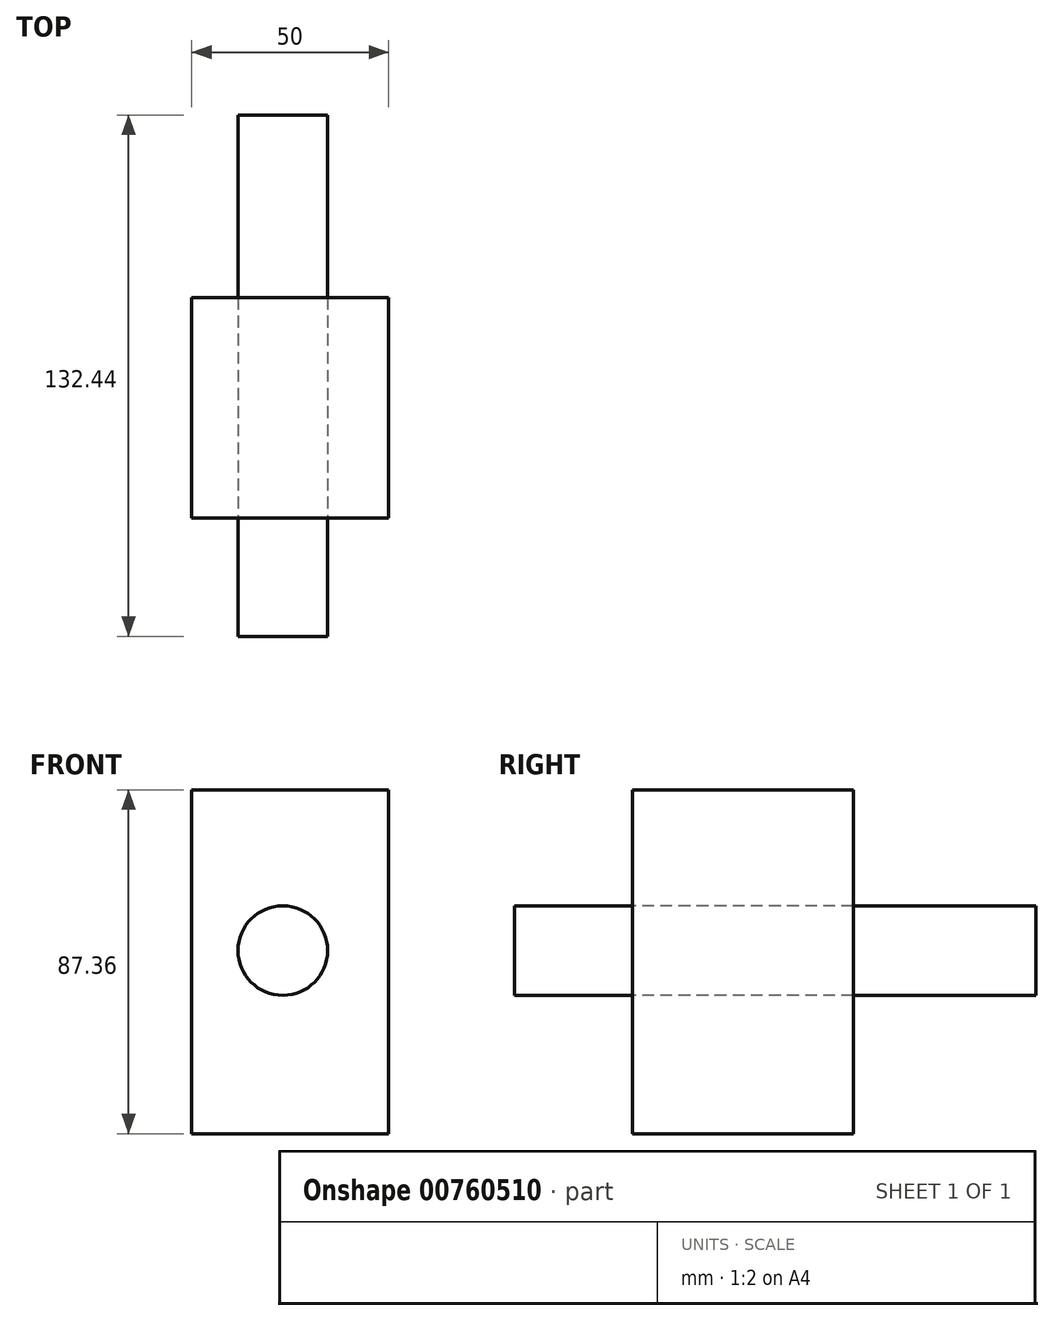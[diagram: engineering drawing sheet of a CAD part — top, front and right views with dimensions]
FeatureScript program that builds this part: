
annotation { "Feature Type Name" : "Feature", "Feature Type Description" : "" }
export const myFeature = defineFeature(function(context is Context, id is Id, definition is map)
    precondition{}
    {
        {
            var Q0;
            Q0=qCreatedBy(makeId("Right.planeOp"),FACE);
            var sketch = newSketch(context, id + "F0", { "sketchPlane" : qUnion([Q0])});
            skLineSegment(sketch, "E0.bottom", {"start": v(-25.06, 35.46) * mm, "end": v(31, 35.46) * mm});
            skLineSegment(sketch, "E0.top", {"start": v(-25.06, -31.9) * mm, "end": v(31, -31.9) * mm});
            skLineSegment(sketch, "E0.left", {"start": v(-25.06, 35.46) * mm, "end": v(-25.06, -31.9) * mm});
            skLineSegment(sketch, "E0.right", {"start": v(31, 35.46) * mm, "end": v(31, -31.9) * mm});
            skSolve(sketch);
        }
        {
            var Q0;
            Q0=makeQuery(id+"F0.imprint","IMPRINT",FACE,{"disambiguationData":[TD([[makeQuery(id+"F0.imprint","IMPRINT",EDGE,{"derivedFrom":sQuery(id+"F0.wireOp",EDGE,"E0.bottom")}),-1.0]])]});
            extrude(context, id + "F1", {"entities" : qUnion([Q0]), "depth" : 50 * mm, "offsetDistance" : 25 * mm});
        }
        {
            var Q0;
            Q0=makeQuery(id+"F1.opExtrude","SWEPT_FACE",FACE,{"disambiguationData":[OSD([sQuery(id+"F0.wireOp",EDGE,"E0.bottom")])]});
            extrude(context, id + "F2", {"entities" : qUnion([Q0]), "operationType" : NewBodyOperationType.ADD, "depth" : 20 * mm, "offsetDistance" : 25 * mm});
        }
        {
            var Q0;
            {var subQ0=sQuery(id+"F0.wireOp",EDGE,"E0.left");Q0=makeQuery(id+"F2.boolean.opBoolean","MERGE",FACE,{"derivedFrom":[makeQuery(id+"F1.opExtrude","SWEPT_FACE",FACE,{"disambiguationData":[OSD([subQ0])]}),makeQuery(id+"F2.opExtrude","SWEPT_FACE",FACE,{"disambiguationData":[OSD([sQuery(id+"F0.wireOp",EDGE,"E0.bottom"),subQ0])]})]});}
            var sketch = newSketch(context, id + "F3", { "sketchPlane" : qUnion([Q0])});
            skCircle(sketch, "E1", {"center": v(23.15, 14.6) * mm, "radius": 11.36 * mm});
            skSolve(sketch);
        }
        {
            var Q0;
            Q0 = qSketchRegion(id + "F3", true);
            extrude(context, id + "F4", {"entities" : qUnion([Q0]), "operationType" : NewBodyOperationType.ADD, "depth" : 30 * mm, "offsetDistance" : 25 * mm});
        }
        {
            var Q0;
            {var subQ0=sQuery(id+"F0.wireOp",EDGE,"E0.left");Q0=makeQuery(id+"F2.boolean.opBoolean","MERGE",FACE,{"derivedFrom":[makeQuery(id+"F1.opExtrude","SWEPT_FACE",FACE,{"disambiguationData":[OSD([subQ0])]}),makeQuery(id+"F2.opExtrude","SWEPT_FACE",FACE,{"disambiguationData":[OSD([sQuery(id+"F0.wireOp",EDGE,"E0.bottom"),subQ0])]})]});}
            var Q1;
            Q1=qCreatedBy(makeId("Front.planeOp"),FACE);
            extrude(context, id + "F5", {"entities" : qUnion([Q0]), "operationType" : NewBodyOperationType.ADD, "endBound" : BoundingType.UP_TO_SURFACE, "oppositeDirection" : true, "depth" : 25 * mm, "endBoundEntityFace" : qUnion([Q1]), "offsetDistance" : 25 * mm});
        }
        {
            var Q0;
            Q0=makeQuery(id+"F4.opExtrude","CAP_FACE",FACE,{"disambiguationData":[OSD([sQuery(id+"F3.wireOp",EDGE,"E1")])],"isStart":false});
            extrude(context, id + "F6", {"entities" : qUnion([Q0]), "endBound" : BoundingType.THROUGH_ALL, "oppositeDirection" : true, "depth" : 25 * mm, "offsetDistance" : 25 * mm});
        }
    });
